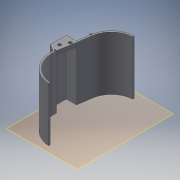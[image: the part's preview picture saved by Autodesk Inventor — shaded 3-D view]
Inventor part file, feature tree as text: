
AUTODESK INVENTOR PART (.ipt)
format: ipt  version: 2017 (Build 210142000, 142)  size: 173,056 bytes
history: native  units: mm
features: other x6, reference x4, plane x2, extrude x2, sketch x2, projected_geometry x1
ambient origin geometry x8: Origin, YZ Plane, XZ Plane, XY Plane, X Axis, Y Axis, Z Axis, Center Point
bodies: Solid1 (feature_tree)
feature tree (17):
  plane  "Work Plane1"
  extrude  "Extrusion1"  Depth=3.0mm
  sketch  "Sketch2"  dims[d2=3.0mm d3=125.0mm d4=0.0mm d5=125.0mm d6=0.0mm]
  plane  "Work Plane2"
  extrude  "Extrusion2"  Depth=125.0mm TaperAngle=0.0deg
  sketch  "Sketch1"  dims[d0=1.0mm d1=3.0mm]
  reference  "Reference1"
  reference  "Reference2"
  projected_geometry  "Projected Loop1"
  reference  "Reference3"
  reference  "Reference4"
  parser-record x1  (decoder bookkeeping rows leaked as tree rows — omitted from the tree; the rows remain in map.json)
  other  "gearbox.iam"
  other  "case part 1:1"
  other  "case bottom half:1"
  other  "fork:1"
  other  "fork:2"
note: 1 file-system path scrubbed to <path> (originals preserved in map.json)
